# Revit family: SB_RFA_RIO_PCD1G3601-A20_PDS
name_source: partatom
category: Generic Models
revit_build: Autodesk Revit 2018 (Build: 20170223_1515(x64)
units: mm (PartAtom-declared; Revit-internal decimal feet)

## family parameters
Can host rebar = No
Cut with Voids When Loaded = No
Host = Face
Part Type = Normal
Room Calculation Point = No
Round Connector Dimension = Use Diameter
Shared = No

## types (1)
- Version1
    Access Clearance Bottom = 20
    Access Clearance Front = 20
    Access Clearance Left = 0
    Access Clearance Rear = 0
    Access Clearance Right = 0
    Access Clearance Top = 20
    Ambient Operation Limits Humidity = 10...80 % r.H.
    Ambient Operation Limits Temperature = 0...+50 °C
    Ambient Storage Limits Temperature = –40…+70 °C
    BIM-object version = -
    Battery Supply = No
    CE Approval = Yes
    Certifications = CE
    Color = Traffic white (RAL 9016)/Sapphire blue RAL5003
    Cut-out = 47x105
    Default Elevation = 1219 mm
    Description = Programmable E-Line input/output module for room automation
    Enclosure Rating = IP65
    Features = Programmable E-Line input/output module for room automation with auxiliary RS-485 interface
    Finish = Matt
    Gross Weight (kg) = 0.21
    Incoming Supply Electrical Voltage = 24
    Incoming Supply Electrical Voltage Tolerance = +20 % / - 15 %
    Incoming Supply Electrical Voltage Type = DC
    Inputs - analogue = 4 analogue inputs 12 bits 0…10 V, ±10 V, 0(4)…20 mA, Pt/Ni 1000, NTC, 0…2500 Ohm, 0…7500 Ohm, 0…300 kOhm
    Inputs - digital = 8 digital inputs 24 VAC/VDC
    Interfaces = 4 interfaces: RS-485 (S-Bus), auxiliary RS-485, USB & NFC (service)
    Location of Manufacturer = 46° 55' 31.28" North, 7° 6' 51.53" East
    Manufacturer = Saia-Burgess Controls AG
    Material = Plastic
    Maximum Power Consumption = typ. 3W
    Model = PCD1.G3601-C15
    Mounting = 35 mm DIN hat rail
    Operations & Maintenance Manual = https://www.sbc-support.com
    Outputs - analogue = 4 triac outputs 24 VCA/1A or 230 VAC/1 A4 
analogue outputs 12 bits, 0…10 V (3 mA max.)
    Outputs - digital = 3 relay changeover 230 VAC / 30 VDC, 6 A, max. inrush current 15 A 1 relay changeover 230 VAC / 30 VDC, 10 A, max. inrush current 65 A
    Overall Depth = 62
    Overall Height = 110
    Overall Witdh = 105
    Porduct Literature = http:\\www.sbc.support.com
    Product Model Number = PCD1.G3601-C15
    Product Range = Saia PCD® E-Line - programmable modules
    Reference Standard = UL
    Shape = Rectangle
    Type = Plastic encased electronic device
    Type Comments = Programmable E-Line input/output module for room automation
    URL = http://www.saia-pcd.com
    Warranty ID = 2 Year from invoice date, max. 30 month from date code

## geometry (parser evidence)
native form markers: Sweep x2
no freeform markers — native parametric forms only
